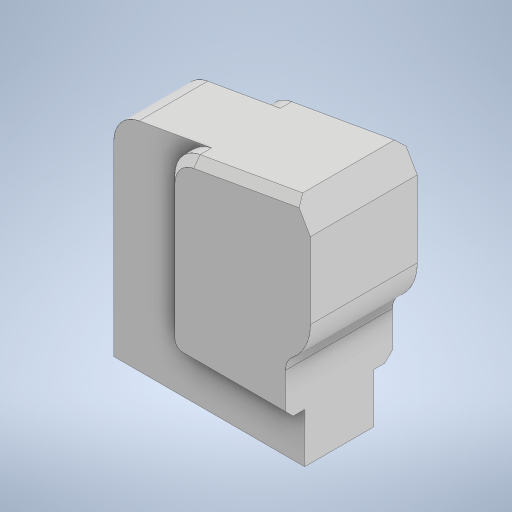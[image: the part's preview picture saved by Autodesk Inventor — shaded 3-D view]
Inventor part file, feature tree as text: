
AUTODESK INVENTOR PART (.ipt)
format: ipt  version: 2024 (Build 280153000, 153)  size: 276,480 bytes
history: native  units: mm
features: fillet x3, extrude x2, sketch x2, chamfer x1, projected_geometry x1
ambient origin geometry x8: Origin, YZ Plane, XZ Plane, XY Plane, X Axis, Y Axis, Z Axis, Center Point
bodies: Solid1 (feature_tree)
feature tree (9):
  extrude  "Extrusion1"  Depth=50.0mm
  fillet  "Fillet1"  Radius=6.0mm
  extrude  "Extrusion2"  Depth=5.0mm
  fillet  "Fillet4"  [1 undecoded]
  fillet  "Fillet3"  Radius=4.0mm
  chamfer  "Chamfer1"  Distance=19.198622mm
  sketch  "Sketch1"  dims[d0=25.0mm d1=50.0mm d2=6.0mm]
  sketch  "Sketch2"  dims[d3=28.0mm d4=0.0mm d5=5.0mm d7=150.0deg d8=4.0mm d9=19.198622mm d11=18.0mm d12=0.0mm d13=38.0mm d14=38.0mm d16=4.0mm d17=8.0mm d18=2.0mm d19=2.0mm d20=45.0deg d21=50.0mm]
  projected_geometry  "Project Cut Edges1"
note: 1 required parameter value undecoded (feature->parameter linkage not recoverable at this tier; creation-order binding heuristic only, values carry confidence <= 0.55)
